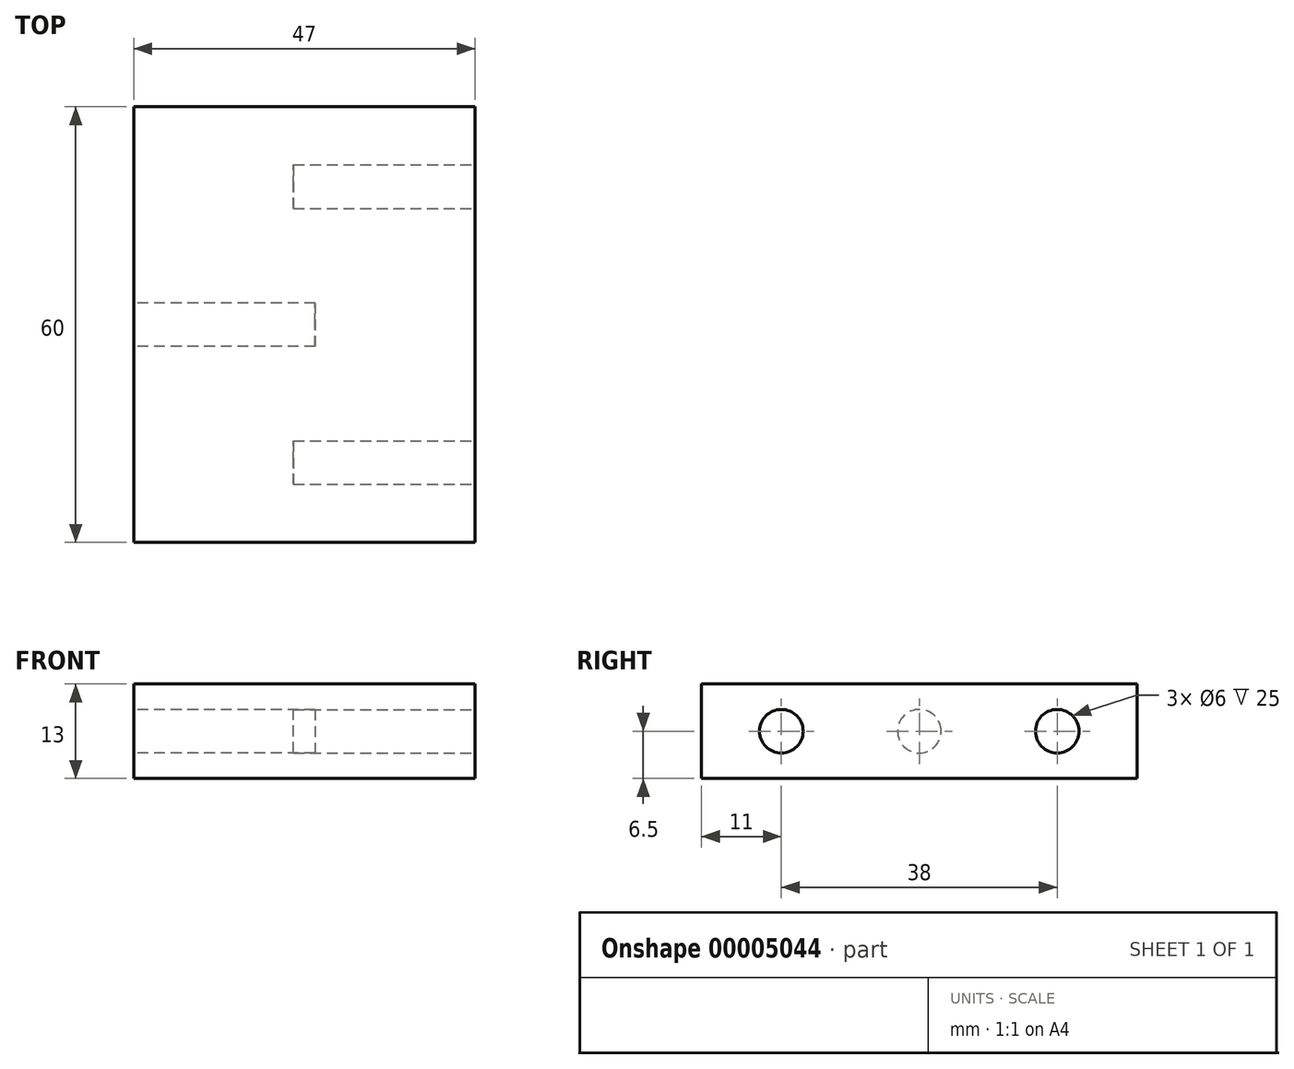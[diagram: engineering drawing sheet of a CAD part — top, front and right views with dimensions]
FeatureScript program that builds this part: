
annotation { "Feature Type Name" : "Feature", "Feature Type Description" : "" }
export const myFeature = defineFeature(function(context is Context, id is Id, definition is map)
    precondition{}
    {
        {
            var Q0;
            Q0=qCreatedBy(makeId("Top.planeOp"),FACE);
            var sketch = newSketch(context, id + "F0", { "sketchPlane" : qUnion([Q0])});
            skLineSegment(sketch, "E0.rect.bottom", {"start": v(23.5, 30) * mm, "end": v(-23.5, 30) * mm});
            skLineSegment(sketch, "E0.rect.top", {"start": v(23.5, -30) * mm, "end": v(-23.5, -30) * mm});
            skLineSegment(sketch, "E0.rect.left", {"start": v(23.5, 30) * mm, "end": v(23.5, -30) * mm});
            skLineSegment(sketch, "E0.rect.right", {"start": v(-23.5, 30) * mm, "end": v(-23.5, -30) * mm});
            skPoint(sketch, "E0.rect.middle", {"position": v(0, 0) * mm});
            skSolve(sketch);
        }
        {
            var Q0;
            Q0 = qSketchRegion(id + "F0", true);
            extrude(context, id + "F1", {"entities" : qUnion([Q0]), "depth" : 13 * mm});
        }
        {
            var Q0;
            Q0=makeQuery(id+"F1.opExtrude","SWEPT_FACE",FACE,{"disambiguationData":[OSD([sQuery(id+"F0.wireOp",EDGE,"E0.rect.left")])]});
            var sketch = newSketch(context, id + "F2", { "sketchPlane" : qUnion([Q0])});
            skCircle(sketch, "E1", {"center": v(-19, 6.5) * mm, "radius": 3 * mm});
            skCircle(sketch, "E2", {"center": v(19, 6.5) * mm, "radius": 3 * mm});
            skSolve(sketch);
        }
        {
            var Q0;
            Q0 = qSketchRegion(id + "F2", true);
            extrude(context, id + "F3", {"entities" : qUnion([Q0]), "operationType" : NewBodyOperationType.REMOVE, "oppositeDirection" : true, "depth" : 25 * mm});
        }
        {
            var Q0;
            Q0=makeQuery(id+"F1.opExtrude","SWEPT_FACE",FACE,{"disambiguationData":[OSD([sQuery(id+"F0.wireOp",EDGE,"E0.rect.right")])]});
            var sketch = newSketch(context, id + "F4", { "sketchPlane" : qUnion([Q0])});
            skLineSegment(sketch, "E3", {"start": v(0, 13) * mm, "end": v(0, 0) * mm});
            skLineSegment(sketch, "E4", {"start": v(30, 6.5) * mm, "end": v(-30, 6.5) * mm});
            skCircle(sketch, "E5", {"center": v(0, 6.5) * mm, "radius": 3 * mm});
            skSolve(sketch);
        }
        {
            var Q0;
            Q0 = qSketchRegion(id + "F4", true);
            extrude(context, id + "F5", {"entities" : qUnion([Q0]), "operationType" : NewBodyOperationType.REMOVE, "oppositeDirection" : true, "depth" : 25 * mm});
        }
    });
